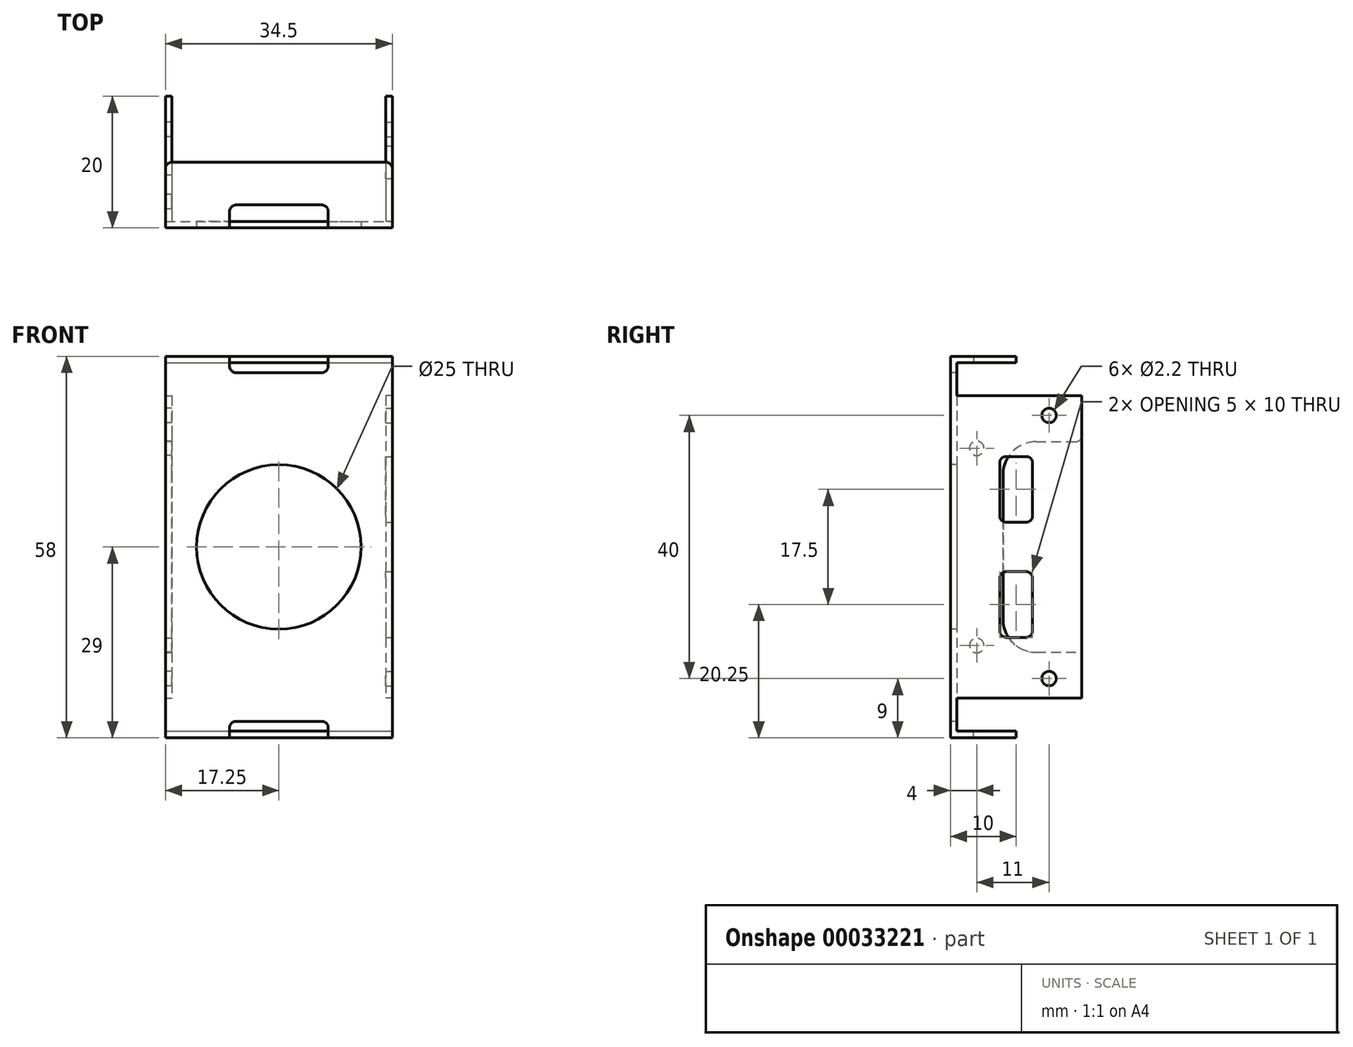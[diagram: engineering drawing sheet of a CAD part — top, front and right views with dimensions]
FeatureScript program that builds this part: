
annotation { "Feature Type Name" : "Feature", "Feature Type Description" : "" }
export const myFeature = defineFeature(function(context is Context, id is Id, definition is map)
    precondition{}
    {
        {
            var Q0;
            Q0=qCreatedBy(makeId("Top.planeOp"),FACE);
            var sketch = newSketch(context, id + "F0", { "sketchPlane" : qUnion([Q0])});
            skLineSegment(sketch, "E0.top", {"start": v(-16.25, -20) * mm, "end": v(16.25, -20) * mm});
            skLineSegment(sketch, "E0.left", {"start": v(-16.25, 20) * mm, "end": v(-16.25, -20) * mm});
            skLineSegment(sketch, "E0.right", {"start": v(16.25, 20) * mm, "end": v(16.25, -20) * mm});
            skPoint(sketch, "E0.middle", {"position": v(0, 0) * mm});
            skLineSegment(sketch, "E1.top", {"start": v(-17.25, -21) * mm, "end": v(17.25, -21) * mm});
            skLineSegment(sketch, "E1.left", {"start": v(-17.25, 20) * mm, "end": v(-17.25, -21) * mm});
            skLineSegment(sketch, "E1.right", {"start": v(17.25, 20) * mm, "end": v(17.25, -21) * mm});
            skLineSegment(sketch, "E2", {"start": v(-16.25, 20) * mm, "end": v(-17.25, 20) * mm});
            skLineSegment(sketch, "E3", {"start": v(16.25, 20) * mm, "end": v(17.25, 20) * mm});
            skPoint(sketch, "E1.bottom.start.orphan", {"position": v(-17.25, 21) * mm});
            skPoint(sketch, "E4.orphan", {"position": v(17.25, 21) * mm});
            skSolve(sketch);
        }
        {
            var Q0;
            Q0 = qSketchRegion(id + "F0", true);
            extrude(context, id + "F1", {"entities" : qUnion([Q0]), "depth" : 56 * mm});
        }
        {
            var Q0;
            Q0=makeQuery(id+"F1.opExtrude","SWEPT_FACE",FACE,{"disambiguationData":[OSD([sQuery(id+"F0.wireOp",EDGE,"E1.left")])]});
            var sketch = newSketch(context, id + "F2", { "sketchPlane" : qUnion([Q0])});
            skLineSegment(sketch, "E5", {"start": v(20, 0) * mm, "end": v(20, 56) * mm, "construction": true});
            skLineSegment(sketch, "E6", {"start": v(-20, 28) * mm, "end": v(20, 28) * mm, "construction": true});
            skLineSegment(sketch, "E7.bottom", {"start": v(20, 0) * mm, "end": v(-20, 0) * mm});
            skLineSegment(sketch, "E7.top", {"start": v(20, 9) * mm, "end": v(-20, 9) * mm});
            skLineSegment(sketch, "E7.left", {"start": v(20, 0) * mm, "end": v(20, 9) * mm});
            skLineSegment(sketch, "E7.right", {"start": v(-20, 0) * mm, "end": v(-20, 9) * mm});
            skLineSegment(sketch, "E8.MirrorCS", {"start": v(-20, 56) * mm, "end": v(-20, 47) * mm});
            skLineSegment(sketch, "E9.MirrorCS", {"start": v(20, 56) * mm, "end": v(20, 47) * mm});
            skLineSegment(sketch, "E10.MirrorCS", {"start": v(20, 47) * mm, "end": v(-20, 47) * mm});
            skLineSegment(sketch, "E11.MirrorCS", {"start": v(20, 56) * mm, "end": v(-20, 56) * mm});
            skCircle(sketch, "E12", {"center": v(18, 43) * mm, "radius": 1.1 * mm});
            skCircle(sketch, "E13", {"center": v(-12, 43) * mm, "radius": 1.1 * mm});
            skCircle(sketch, "E14.MirrorC", {"center": v(-12, 13) * mm, "radius": 1.1 * mm});
            skCircle(sketch, "E15.MirrorC", {"center": v(18, 13) * mm, "radius": 1.1 * mm});
            skLineSegment(sketch, "E16.bottom", {"start": v(-20, 47) * mm, "end": v(-16, 47) * mm});
            skLineSegment(sketch, "E16.top", {"start": v(-20, 9) * mm, "end": v(-16, 9) * mm});
            skLineSegment(sketch, "E16.left", {"start": v(-20, 47) * mm, "end": v(-20, 9) * mm});
            skLineSegment(sketch, "E16.right", {"start": v(-16, 47) * mm, "end": v(-16, 9) * mm});
            skLineSegment(sketch, "E17", {"start": v(-12, 13) * mm, "end": v(18, 13) * mm, "construction": true});
            skPoint(sketch, "E18", {"position": v(3, 13) * mm});
            skCircle(sketch, "E19", {"center": v(3, 28) * mm, "radius": 12.5 * mm});
            skSolve(sketch);
        }
        {
            var Q0;
            Q0 = qSketchRegion(id + "F2", true);
            extrude(context, id + "F3", {"entities" : qUnion([Q0]), "operationType" : NewBodyOperationType.REMOVE, "endBound" : BoundingType.UP_TO_NEXT, "oppositeDirection" : true, "depth" : 25 * mm});
        }
        {
            var Q0;
            Q0=makeQuery(id+"F1.opExtrude","SWEPT_FACE",FACE,{"disambiguationData":[OSD([sQuery(id+"F0.wireOp",EDGE,"E1.right")])]});
            var sketch = newSketch(context, id + "F4", { "sketchPlane" : qUnion([Q0])});
            skLineSegment(sketch, "E20", {"start": v(-20, 0) * mm, "end": v(-20, 56) * mm, "construction": true});
            skLineSegment(sketch, "E21.bottom", {"start": v(20, 0) * mm, "end": v(-1, 0) * mm});
            skLineSegment(sketch, "E21.top", {"start": v(20, 56) * mm, "end": v(-1, 56) * mm});
            skLineSegment(sketch, "E21.left", {"start": v(20, 0) * mm, "end": v(20, 56) * mm});
            skLineSegment(sketch, "E21.right", {"start": v(-1, 0) * mm, "end": v(-1, 56) * mm});
            skLineSegment(sketch, "E22", {"start": v(20, 28) * mm, "end": v(-20, 28) * mm, "construction": true});
            skCircle(sketch, "E23", {"center": v(-6, 8) * mm, "radius": 1.1 * mm});
            skCircle(sketch, "E24.MirrorC", {"center": v(-6, 48) * mm, "radius": 1.1 * mm});
            skSolve(sketch);
        }
        {
            var Q0;
            Q0 = qSketchRegion(id + "F4", true);
            extrude(context, id + "F5", {"entities" : qUnion([Q0]), "operationType" : NewBodyOperationType.REMOVE, "endBound" : BoundingType.UP_TO_NEXT, "oppositeDirection" : true, "depth" : 25 * mm});
        }
        {
            var Q0;
            Q0=makeQuery(id+"F1.opExtrude","SWEPT_FACE",FACE,{"disambiguationData":[OSD([sQuery(id+"F0.wireOp",EDGE,"E1.right")])]});
            var sketch = newSketch(context, id + "F6", { "sketchPlane" : qUnion([Q0])});
            skLineSegment(sketch, "E25.bottom", {"start": v(-1, 0) * mm, "end": v(-21, 0) * mm});
            skLineSegment(sketch, "E25.top", {"start": v(-1, 5) * mm, "end": v(-21, 5) * mm});
            skLineSegment(sketch, "E25.left", {"start": v(-1, 0) * mm, "end": v(-1, 5) * mm});
            skLineSegment(sketch, "E25.right", {"start": v(-21, 0) * mm, "end": v(-21, 5) * mm});
            skPoint(sketch, "E26", {"position": v(-6, 8) * mm});
            skLineSegment(sketch, "E27", {"start": v(-21, 28) * mm, "end": v(-1, 28) * mm, "construction": true});
            skLineSegment(sketch, "E28.MirrorCS", {"start": v(-21, 56) * mm, "end": v(-21, 51) * mm});
            skLineSegment(sketch, "E29.MirrorCS", {"start": v(-1, 56) * mm, "end": v(-1, 51) * mm});
            skLineSegment(sketch, "E30.MirrorCS", {"start": v(-1, 51) * mm, "end": v(-21, 51) * mm});
            skLineSegment(sketch, "E31.MirrorCS", {"start": v(-1, 56) * mm, "end": v(-21, 56) * mm});
            skSolve(sketch);
        }
        {
            var Q0;
            Q0 = qSketchRegion(id + "F6", true);
            extrude(context, id + "F7", {"entities" : qUnion([Q0]), "operationType" : NewBodyOperationType.REMOVE, "oppositeDirection" : true, "depth" : 1 * mm});
        }
        {
            var Q0;
            Q0=makeQuery(id+"F1.opExtrude","SWEPT_FACE",FACE,{"disambiguationData":[OSD([sQuery(id+"F0.wireOp",EDGE,"E1.left")])]});
            var sketch = newSketch(context, id + "F8", { "sketchPlane" : qUnion([Q0])});
            skLineSegment(sketch, "E32.bottom", {"start": v(-16, 47) * mm, "end": v(20, 47) * mm});
            skLineSegment(sketch, "E32.top", {"start": v(-16, 9) * mm, "end": v(20, 9) * mm});
            skLineSegment(sketch, "E32.left", {"start": v(-16, 47) * mm, "end": v(-16, 9) * mm});
            skLineSegment(sketch, "E32.right", {"start": v(20, 47) * mm, "end": v(20, 9) * mm});
            skSolve(sketch);
        }
        {
            var Q0;
            Q0 = qSketchRegion(id + "F8", true);
            extrude(context, id + "F9", {"entities" : qUnion([Q0]), "operationType" : NewBodyOperationType.REMOVE, "oppositeDirection" : true, "depth" : 1 * mm});
        }
        {
            var Q0;
            Q0=makeQuery(id+"F1.opExtrude","SWEPT_BODY",BODY,{"disambiguationData":[OSD([sQuery(id+"F0.wireOp",EDGE,"E0.top"),sQuery(id+"F0.wireOp",EDGE,"E0.left"),sQuery(id+"F0.wireOp",EDGE,"E0.right"),sQuery(id+"F0.wireOp",EDGE,"E1.top"),sQuery(id+"F0.wireOp",EDGE,"E1.left"),sQuery(id+"F0.wireOp",EDGE,"E1.right"),sQuery(id+"F0.wireOp",EDGE,"E2"),sQuery(id+"F0.wireOp",EDGE,"E3")])]});
            var Q1;
            Q1=qCreatedBy(makeId("Right.planeOp"),FACE);
            mirror(context, id + "F10", {"operationType" : NewBodyOperationType.ADD, "entities" : qUnion([Q0]), "mirrorPlane" : qUnion([Q1])});
        }
        {
            var Q0;
            Q0=makeQuery(id+"F10.boolean.opBoolean","MERGE",FACE,{"derivedFrom":[makeQuery(id+"F1.opExtrude","SWEPT_FACE",FACE,{"disambiguationData":[OSD([sQuery(id+"F0.wireOp",EDGE,"E1.left")])]}),makeQuery(id+"F10.opPattern","COPY",FACE,{"derivedFrom":makeQuery(id+"F1.opExtrude","SWEPT_FACE",FACE,{"disambiguationData":[OSD([sQuery(id+"F0.wireOp",EDGE,"E1.right")])]}),"instanceName":"1"})]});
            var sketch = newSketch(context, id + "F11", { "sketchPlane" : qUnion([Q0])});
            skLineSegment(sketch, "E33", {"start": v(21, 28) * mm, "end": v(1, 28) * mm, "construction": true});
            skCircle(sketch, "E34", {"center": v(17, 43) * mm, "radius": 1.1 * mm});
            skCircle(sketch, "E35.MirrorC", {"center": v(17, 13) * mm, "radius": 1.1 * mm});
            skLineSegment(sketch, "E36.bottom", {"start": v(13, 44) * mm, "end": v(1, 44) * mm});
            skLineSegment(sketch, "E36.top", {"start": v(13, 12) * mm, "end": v(1, 12) * mm});
            skLineSegment(sketch, "E36.left", {"start": v(13, 44) * mm, "end": v(13, 12) * mm});
            skLineSegment(sketch, "E36.right", {"start": v(1, 44) * mm, "end": v(1, 12) * mm});
            skPoint(sketch, "E37", {"position": v(6, 48) * mm});
            skPoint(sketch, "E38", {"position": v(13, 28) * mm});
            skSolve(sketch);
        }
        {
            var Q0;
            Q0 = qSketchRegion(id + "F11", true);
            extrude(context, id + "F12", {"entities" : qUnion([Q0]), "operationType" : NewBodyOperationType.REMOVE, "endBound" : BoundingType.UP_TO_NEXT, "oppositeDirection" : true, "depth" : 25 * mm});
        }
        {
            var Q0;
            {var subQ0=makeQuery(id+"F1.opExtrude","SWEPT_FACE",FACE,{"disambiguationData":[OSD([sQuery(id+"F0.wireOp",EDGE,"E1.top")])]});Q0=makeQuery(id+"F10.boolean.opBoolean","MERGE",FACE,{"derivedFrom":[subQ0,makeQuery(id+"F10.opPattern","COPY",FACE,{"derivedFrom":subQ0,"instanceName":"1"})]});}
            var sketch = newSketch(context, id + "F13", { "sketchPlane" : qUnion([Q0])});
            skLineSegment(sketch, "E39.bottom", {"start": v(17.25, 0) * mm, "end": v(-17.25, 0) * mm});
            skLineSegment(sketch, "E39.top", {"start": v(17.25, -1) * mm, "end": v(-17.25, -1) * mm});
            skLineSegment(sketch, "E39.left", {"start": v(17.25, 0) * mm, "end": v(17.25, -1) * mm});
            skLineSegment(sketch, "E39.right", {"start": v(-17.25, 0) * mm, "end": v(-17.25, -1) * mm});
            skLineSegment(sketch, "E40", {"start": v(17.25, 28) * mm, "end": v(-17.25, 28) * mm, "construction": true});
            skLineSegment(sketch, "E41.MirrorCS", {"start": v(17.25, 56) * mm, "end": v(17.25, 57) * mm});
            skLineSegment(sketch, "E42.MirrorCS", {"start": v(-17.25, 56) * mm, "end": v(-17.25, 57) * mm});
            skLineSegment(sketch, "E43.MirrorCS", {"start": v(17.25, 56) * mm, "end": v(-17.25, 56) * mm});
            skLineSegment(sketch, "E44.MirrorCS", {"start": v(17.25, 57) * mm, "end": v(-17.25, 57) * mm});
            skSolve(sketch);
        }
        {
            var Q0;
            Q0 = qSketchRegion(id + "F13", true);
            extrude(context, id + "F14", {"entities" : qUnion([Q0]), "operationType" : NewBodyOperationType.ADD, "oppositeDirection" : true, "depth" : 10 * mm});
        }
        {
            var Q0;
            {var subQ0=makeQuery(id+"F1.opExtrude","SWEPT_FACE",FACE,{"disambiguationData":[OSD([sQuery(id+"F0.wireOp",EDGE,"E1.top")])]});Q0=makeQuery(id+"F14.boolean.opBoolean","MERGE",FACE,{"derivedFrom":[makeQuery(id+"F10.boolean.opBoolean","MERGE",FACE,{"derivedFrom":[subQ0,makeQuery(id+"F10.opPattern","COPY",FACE,{"derivedFrom":subQ0,"instanceName":"1"})]}),makeQuery(id+"F14.opExtrude","CAP_FACE",FACE,{"disambiguationData":[OSD([sQuery(id+"F13.wireOp",EDGE,"E39.bottom"),sQuery(id+"F13.wireOp",EDGE,"E39.top"),sQuery(id+"F13.wireOp",EDGE,"E39.left"),sQuery(id+"F13.wireOp",EDGE,"E39.right")])],"isStart":true}),makeQuery(id+"F14.opExtrude","CAP_FACE",FACE,{"disambiguationData":[OSD([sQuery(id+"F13.wireOp",EDGE,"E41.MirrorCS"),sQuery(id+"F13.wireOp",EDGE,"E42.MirrorCS"),sQuery(id+"F13.wireOp",EDGE,"E43.MirrorCS"),sQuery(id+"F13.wireOp",EDGE,"E44.MirrorCS")])],"isStart":true})]});}
            var sketch = newSketch(context, id + "F15", { "sketchPlane" : qUnion([Q0])});
            skCircle(sketch, "E45", {"center": v(0, 28) * mm, "radius": 12.5 * mm});
            skPoint(sketch, "E46", {"position": v(-17.25, 28) * mm});
            skLineSegment(sketch, "E47.bottom", {"start": v(-7.5, 59.5) * mm, "end": v(7.5, 59.5) * mm});
            skLineSegment(sketch, "E47.top", {"start": v(-7.5, 54.5) * mm, "end": v(7.5, 54.5) * mm});
            skLineSegment(sketch, "E47.left", {"start": v(-7.5, 59.5) * mm, "end": v(-7.5, 54.5) * mm});
            skLineSegment(sketch, "E47.right", {"start": v(7.5, 59.5) * mm, "end": v(7.5, 54.5) * mm});
            skPoint(sketch, "E47.middle", {"position": v(0, 57) * mm});
            skLineSegment(sketch, "E48", {"start": v(-17.25, 28) * mm, "end": v(17.25, 28) * mm, "construction": true});
            skLineSegment(sketch, "E49.MirrorCS", {"start": v(-7.5, -3.5) * mm, "end": v(-7.5, 1.5) * mm});
            skLineSegment(sketch, "E50.MirrorCS", {"start": v(7.5, -3.5) * mm, "end": v(7.5, 1.5) * mm});
            skLineSegment(sketch, "E51.MirrorCS", {"start": v(-7.5, -3.5) * mm, "end": v(7.5, -3.5) * mm});
            skLineSegment(sketch, "E52.MirrorCS", {"start": v(-7.5, 1.5) * mm, "end": v(7.5, 1.5) * mm});
            skPoint(sketch, "E53.MirrorP", {"position": v(0, -1) * mm});
            skSolve(sketch);
        }
        {
            var Q0;
            Q0 = qSketchRegion(id + "F15", true);
            extrude(context, id + "F16", {"entities" : qUnion([Q0]), "operationType" : NewBodyOperationType.REMOVE, "oppositeDirection" : true, "depth" : 3.5 * mm});
        }
        {
            var Q0;
            Q0=makeQuery(id+"F14.boolean.opBoolean","MERGE",FACE,{"derivedFrom":[makeQuery(id+"F10.boolean.opBoolean","MERGE",FACE,{"derivedFrom":[makeQuery(id+"F1.opExtrude","SWEPT_FACE",FACE,{"disambiguationData":[OSD([sQuery(id+"F0.wireOp",EDGE,"E1.right")])]}),makeQuery(id+"F10.opPattern","COPY",FACE,{"derivedFrom":makeQuery(id+"F1.opExtrude","SWEPT_FACE",FACE,{"disambiguationData":[OSD([sQuery(id+"F0.wireOp",EDGE,"E1.left")])]}),"instanceName":"1"})]}),makeQuery(id+"F14.opExtrude","SWEPT_FACE",FACE,{"disambiguationData":[OSD([sQuery(id+"F13.wireOp",EDGE,"E39.left")])]}),makeQuery(id+"F14.opExtrude","SWEPT_FACE",FACE,{"disambiguationData":[OSD([sQuery(id+"F13.wireOp",EDGE,"E41.MirrorCS")])]})]});
            var sketch = newSketch(context, id + "F17", { "sketchPlane" : qUnion([Q0])});
            skLineSegment(sketch, "E54", {"start": v(-21, 28) * mm, "end": v(-1, 28) * mm, "construction": true});
            skLineSegment(sketch, "E55.bottom", {"start": v(-12.5, 14.25) * mm, "end": v(-9.5, 14.25) * mm});
            skLineSegment(sketch, "E55.top", {"start": v(-12.5, 24.25) * mm, "end": v(-9.5, 24.25) * mm});
            skLineSegment(sketch, "E55.left", {"start": v(-13.5, 15.25) * mm, "end": v(-13.5, 23.25) * mm});
            skLineSegment(sketch, "E55.right", {"start": v(-8.5, 15.25) * mm, "end": v(-8.5, 23.25) * mm});
            skPoint(sketch, "E55.middle", {"position": v(-11, 19.25) * mm});
            skPoint(sketch, "E56", {"position": v(-6, 8) * mm});
            skPoint(sketch, "E57.visualSharp", {"position": v(-13.5, 14.25) * mm});
            skArc(sketch, "E57.filletArc", {"start": v(-13.5, 15.25) * mm, "mid": v(-13.2, 14.54) * mm, "end": v(-12.5, 14.25) * mm});
            skPoint(sketch, "E58.visualSharp", {"position": v(-8.5, 14.25) * mm});
            skArc(sketch, "E58.filletArc", {"start": v(-9.5, 14.25) * mm, "mid": v(-8.8, 14.54) * mm, "end": v(-8.5, 15.25) * mm});
            skPoint(sketch, "E59.visualSharp", {"position": v(-13.5, 24.25) * mm});
            skArc(sketch, "E59.filletArc", {"start": v(-12.5, 24.25) * mm, "mid": v(-13.2, 23.96) * mm, "end": v(-13.5, 23.25) * mm});
            skPoint(sketch, "E60.visualSharp", {"position": v(-8.5, 24.25) * mm});
            skArc(sketch, "E60.filletArc", {"start": v(-8.5, 23.25) * mm, "mid": v(-8.8, 23.96) * mm, "end": v(-9.5, 24.25) * mm});
            skArc(sketch, "E61.MirrorCS", {"start": v(-13.5, 40.75) * mm, "mid": v(-13.2, 41.46) * mm, "end": v(-12.5, 41.75) * mm});
            skArc(sketch, "E62.MirrorCS", {"start": v(-9.5, 41.75) * mm, "mid": v(-8.8, 41.46) * mm, "end": v(-8.5, 40.75) * mm});
            skArc(sketch, "E63.MirrorCS", {"start": v(-12.5, 31.75) * mm, "mid": v(-13.2, 32.04) * mm, "end": v(-13.5, 32.75) * mm});
            skArc(sketch, "E64.MirrorCS", {"start": v(-8.5, 32.75) * mm, "mid": v(-8.8, 32.04) * mm, "end": v(-9.5, 31.75) * mm});
            skLineSegment(sketch, "E65.MirrorCS", {"start": v(-8.5, 40.75) * mm, "end": v(-8.5, 32.75) * mm});
            skLineSegment(sketch, "E66.MirrorCS", {"start": v(-13.5, 40.75) * mm, "end": v(-13.5, 32.75) * mm});
            skLineSegment(sketch, "E67.MirrorCS", {"start": v(-12.5, 31.75) * mm, "end": v(-9.5, 31.75) * mm});
            skLineSegment(sketch, "E68.MirrorCS", {"start": v(-12.5, 41.75) * mm, "end": v(-9.5, 41.75) * mm});
            skPoint(sketch, "E69.MirrorP", {"position": v(-11, 36.75) * mm});
            skPoint(sketch, "E70.MirrorP", {"position": v(-13.5, 41.75) * mm});
            skPoint(sketch, "E71.MirrorP", {"position": v(-8.5, 41.75) * mm});
            skPoint(sketch, "E72.MirrorP", {"position": v(-8.5, 31.75) * mm});
            skPoint(sketch, "E73.MirrorP", {"position": v(-13.5, 31.75) * mm});
            skSolve(sketch);
        }
        {
            var Q0;
            Q0 = qSketchRegion(id + "F17", true);
            extrude(context, id + "F18", {"entities" : qUnion([Q0]), "operationType" : NewBodyOperationType.REMOVE, "endBound" : BoundingType.UP_TO_NEXT, "oppositeDirection" : true, "depth" : 25 * mm});
        }
        {
            var Q0;
            Q0=makeQuery(id+"F14.opExtrude","CAP_EDGE",EDGE,{"disambiguationData":[OSD([sQuery(id+"F13.wireOp",EDGE,"E42.MirrorCS")])],"isStart":false});
            var Q1;
            Q1=makeQuery(id+"F14.opExtrude","CAP_EDGE",EDGE,{"disambiguationData":[OSD([sQuery(id+"F13.wireOp",EDGE,"E41.MirrorCS")])],"isStart":false});
            var Q2;
            Q2=makeQuery(id+"F7.boolean.opBoolean","COPY",EDGE,{"derivedFrom":makeQuery(id+"F7.opExtrude","SWEPT_EDGE",EDGE,{"disambiguationData":[OSD([sQuery(id+"F4.wireOp",EDGE,"E21.right"),sQuery(id+"F6.wireOp",EDGE,"E29.MirrorCS"),sQuery(id+"F6.wireOp",EDGE,"E30.MirrorCS")])]})});
            var Q3;
            Q3=makeQuery(id+"F7.boolean.opBoolean","COPY",EDGE,{"derivedFrom":makeQuery(id+"F7.opExtrude","SWEPT_EDGE",EDGE,{"disambiguationData":[OSD([sQuery(id+"F4.wireOp",EDGE,"E21.right"),sQuery(id+"F6.wireOp",EDGE,"E25.top"),sQuery(id+"F6.wireOp",EDGE,"E25.left")])]})});
            var Q4;
            Q4=makeQuery(id+"F10.opPattern","COPY",EDGE,{"derivedFrom":makeQuery(id+"F7.boolean.opBoolean","COPY",EDGE,{"derivedFrom":makeQuery(id+"F7.opExtrude","SWEPT_EDGE",EDGE,{"disambiguationData":[OSD([sQuery(id+"F4.wireOp",EDGE,"E21.right"),sQuery(id+"F6.wireOp",EDGE,"E25.top"),sQuery(id+"F6.wireOp",EDGE,"E25.left")])]})}),"instanceName":"1"});
            var Q5;
            Q5=makeQuery(id+"F12.boolean.opBoolean","COPY",EDGE,{"derivedFrom":makeQuery(id+"F12.opExtrude","SWEPT_EDGE",EDGE,{"disambiguationData":[OSD([sQuery(id+"F4.wireOp",EDGE,"E21.right"),sQuery(id+"F11.wireOp",EDGE,"E36.top"),sQuery(id+"F11.wireOp",EDGE,"E36.right")])]})});
            var Q6;
            Q6=makeQuery(id+"F10.opPattern","COPY",EDGE,{"derivedFrom":makeQuery(id+"F7.boolean.opBoolean","COPY",EDGE,{"derivedFrom":makeQuery(id+"F7.opExtrude","SWEPT_EDGE",EDGE,{"disambiguationData":[OSD([sQuery(id+"F4.wireOp",EDGE,"E21.right"),sQuery(id+"F6.wireOp",EDGE,"E29.MirrorCS"),sQuery(id+"F6.wireOp",EDGE,"E30.MirrorCS")])]})}),"instanceName":"1"});
            var Q7;
            Q7=makeQuery(id+"F12.boolean.opBoolean","COPY",EDGE,{"derivedFrom":makeQuery(id+"F12.opExtrude","SWEPT_EDGE",EDGE,{"disambiguationData":[OSD([sQuery(id+"F4.wireOp",EDGE,"E21.right"),sQuery(id+"F11.wireOp",EDGE,"E36.bottom"),sQuery(id+"F11.wireOp",EDGE,"E36.right")])]})});
            var Q8;
            Q8=makeQuery(id+"F14.opExtrude","CAP_EDGE",EDGE,{"disambiguationData":[OSD([sQuery(id+"F13.wireOp",EDGE,"E39.right")])],"isStart":false});
            var Q9;
            Q9=makeQuery(id+"F14.opExtrude","CAP_EDGE",EDGE,{"disambiguationData":[OSD([sQuery(id+"F13.wireOp",EDGE,"E39.left")])],"isStart":false});
            var Q10;
            Q10=makeQuery(id+"F16.boolean.opBoolean","COPY",EDGE,{"derivedFrom":makeQuery(id+"F16.opExtrude","SWEPT_EDGE",EDGE,{"disambiguationData":[OSD([sQuery(id+"F15.wireOp",EDGE,"E50.MirrorCS"),sQuery(id+"F15.wireOp",EDGE,"E52.MirrorCS")])]})});
            var Q11;
            Q11=makeQuery(id+"F16.boolean.opBoolean","COPY",EDGE,{"derivedFrom":makeQuery(id+"F16.opExtrude","CAP_EDGE",EDGE,{"disambiguationData":[OSD([sQuery(id+"F15.wireOp",EDGE,"E50.MirrorCS")])],"isStart":false})});
            var Q12;
            Q12=makeQuery(id+"F16.boolean.opBoolean","COPY",EDGE,{"derivedFrom":makeQuery(id+"F16.opExtrude","SWEPT_EDGE",EDGE,{"disambiguationData":[OSD([sQuery(id+"F15.wireOp",EDGE,"E49.MirrorCS"),sQuery(id+"F15.wireOp",EDGE,"E52.MirrorCS")])]})});
            var Q13;
            Q13=makeQuery(id+"F16.boolean.opBoolean","COPY",EDGE,{"derivedFrom":makeQuery(id+"F16.opExtrude","CAP_EDGE",EDGE,{"disambiguationData":[OSD([sQuery(id+"F15.wireOp",EDGE,"E49.MirrorCS")])],"isStart":false})});
            var Q14;
            Q14=makeQuery(id+"F16.boolean.opBoolean","COPY",EDGE,{"derivedFrom":makeQuery(id+"F16.opExtrude","SWEPT_EDGE",EDGE,{"disambiguationData":[OSD([sQuery(id+"F15.wireOp",EDGE,"E47.top"),sQuery(id+"F15.wireOp",EDGE,"E47.right")])]})});
            var Q15;
            Q15=makeQuery(id+"F16.boolean.opBoolean","COPY",EDGE,{"derivedFrom":makeQuery(id+"F16.opExtrude","CAP_EDGE",EDGE,{"disambiguationData":[OSD([sQuery(id+"F15.wireOp",EDGE,"E47.right")])],"isStart":false})});
            var Q16;
            Q16=makeQuery(id+"F16.boolean.opBoolean","COPY",EDGE,{"derivedFrom":makeQuery(id+"F16.opExtrude","CAP_EDGE",EDGE,{"disambiguationData":[OSD([sQuery(id+"F15.wireOp",EDGE,"E47.left")])],"isStart":false})});
            var Q17;
            Q17=makeQuery(id+"F16.boolean.opBoolean","COPY",EDGE,{"derivedFrom":makeQuery(id+"F16.opExtrude","SWEPT_EDGE",EDGE,{"disambiguationData":[OSD([sQuery(id+"F15.wireOp",EDGE,"E47.top"),sQuery(id+"F15.wireOp",EDGE,"E47.left")])]})});
            fillet(context, id + "F19", {"entities" : qUnion([Q0, Q1, Q2, Q3, Q4, Q5, Q6, Q7, Q8, Q9, Q10, Q11, Q12, Q13, Q14, Q15, Q16, Q17]), "radius" : 1 * mm, "tangentPropagation" : true, "allowEdgeOverflow" : false});
        }
        {
            var Q0;
            Q0=makeQuery(id+"F12.boolean.opBoolean","COPY",EDGE,{"derivedFrom":makeQuery(id+"F12.opExtrude","SWEPT_EDGE",EDGE,{"disambiguationData":[OSD([sQuery(id+"F11.wireOp",EDGE,"E36.bottom"),sQuery(id+"F11.wireOp",EDGE,"E36.left")])]})});
            var Q1;
            Q1=makeQuery(id+"F12.boolean.opBoolean","COPY",EDGE,{"derivedFrom":makeQuery(id+"F12.opExtrude","SWEPT_EDGE",EDGE,{"disambiguationData":[OSD([sQuery(id+"F11.wireOp",EDGE,"E36.top"),sQuery(id+"F11.wireOp",EDGE,"E36.left")])]})});
            fillet(context, id + "F20", {"entities" : qUnion([Q0, Q1]), "radius" : 5 * mm, "tangentPropagation" : true, "allowEdgeOverflow" : false});
        }
    });
